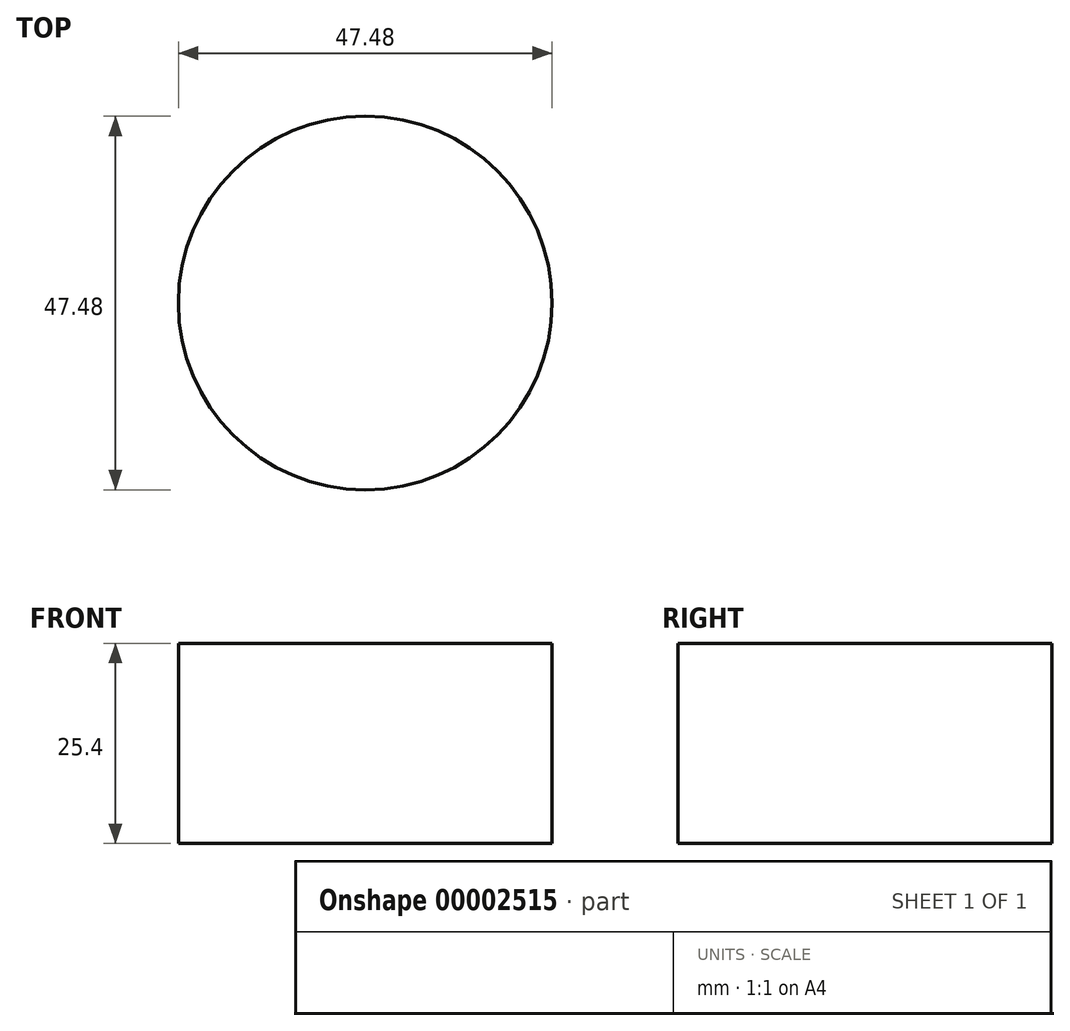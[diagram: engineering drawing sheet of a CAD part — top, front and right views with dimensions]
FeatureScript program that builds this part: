
annotation { "Feature Type Name" : "Feature", "Feature Type Description" : "" }
export const myFeature = defineFeature(function(context is Context, id is Id, definition is map)
    precondition{}
    {
        {
            var Q0;
            Q0=qCreatedBy(makeId("Top.planeOp"),FACE);
            var sketch = newSketch(context, id + "F0", { "sketchPlane" : qUnion([Q0])});
            skCircle(sketch, "E0", {"center": v(0, 0) * mm, "radius": 23.74 * mm});
            skSolve(sketch);
        }
        {
            var Q0;
            Q0 = qSketchRegion(id + "F0", true);
            extrude(context, id + "F1", {"entities" : qUnion([Q0]), "depth" : 25.4 * mm});
        }
    });
